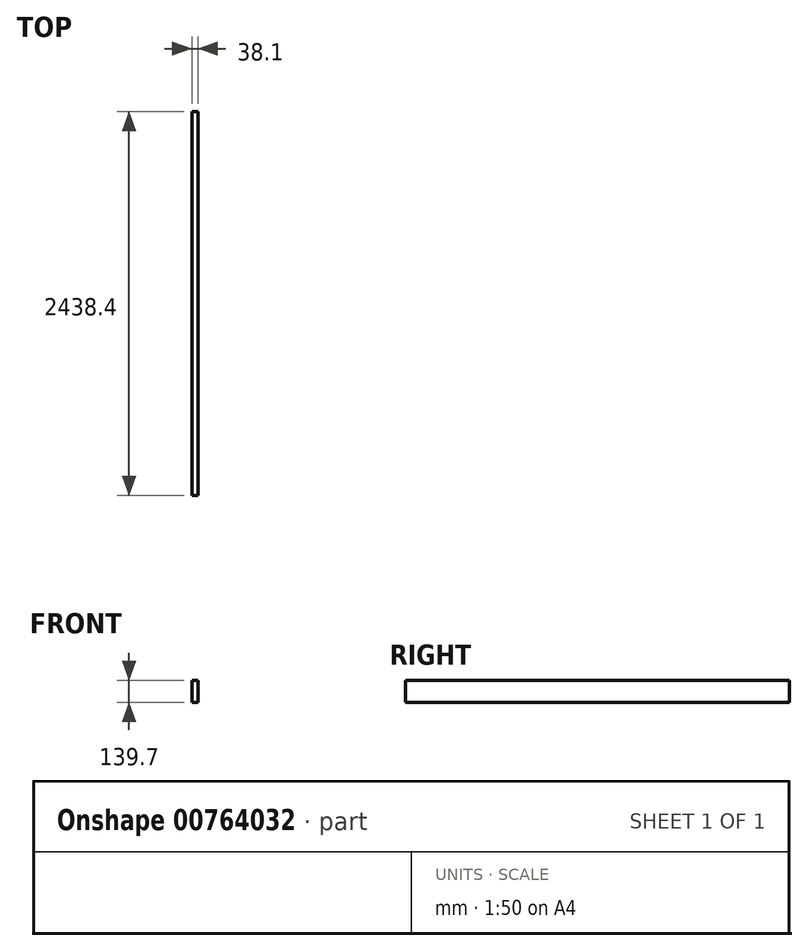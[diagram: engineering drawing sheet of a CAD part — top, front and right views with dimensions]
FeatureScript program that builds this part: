
annotation { "Feature Type Name" : "Feature", "Feature Type Description" : "" }
export const myFeature = defineFeature(function(context is Context, id is Id, definition is map)
    precondition{}
    {
        {
            var Q0;
            Q0=qCreatedBy(makeId("Front.planeOp"),FACE);
            var sketch = newSketch(context, id + "F0", { "sketchPlane" : qUnion([Q0])});
            skLineSegment(sketch, "E0.bottom", {"start": v(0, 0) * mm, "end": v(38.1, 0) * mm});
            skLineSegment(sketch, "E0.top", {"start": v(0, 139.7) * mm, "end": v(38.1, 139.7) * mm});
            skLineSegment(sketch, "E0.left", {"start": v(0, 0) * mm, "end": v(0, 139.7) * mm});
            skLineSegment(sketch, "E0.right", {"start": v(38.1, 0) * mm, "end": v(38.1, 139.7) * mm});
            skSolve(sketch);
        }
        {
            var Q0;
            Q0=makeQuery(id+"F0.imprint","IMPRINT",FACE,{"disambiguationData":[TD([[makeQuery(id+"F0.imprint","IMPRINT",EDGE,{"derivedFrom":sQuery(id+"F0.wireOp",EDGE,"E0.bottom")}),1.0]])]});
            extrude(context, id + "F1", {"entities" : qUnion([Q0]), "depth" : 2438.4 * mm, "offsetDistance" : 25.4 * mm});
        }
    });
